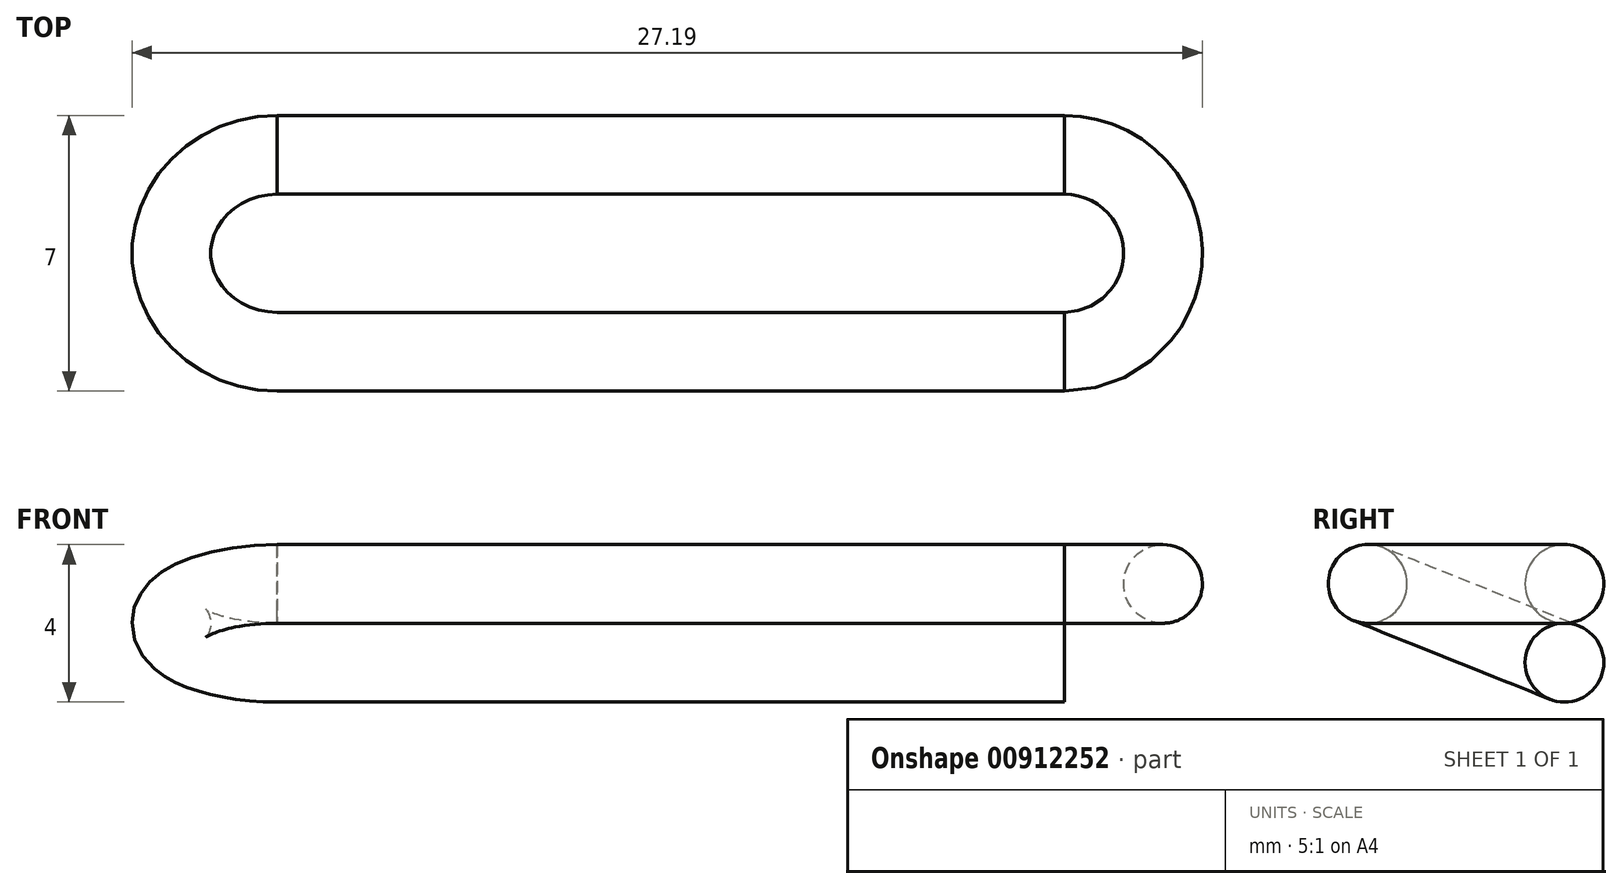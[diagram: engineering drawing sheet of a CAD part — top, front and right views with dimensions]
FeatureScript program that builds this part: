
annotation { "Feature Type Name" : "Feature", "Feature Type Description" : "" }
export const myFeature = defineFeature(function(context is Context, id is Id, definition is map)
    precondition{}
    {
        {
            var Q0;
            Q0=qCreatedBy(makeId("Top.planeOp"),FACE);
            var sketch = newSketch(context, id + "F0", { "sketchPlane" : qUnion([Q0])});
            skCircle(sketch, "E0", {"center": v(-10, 0) * mm, "radius": 2.5 * mm, "construction": true});
            skCircle(sketch, "E1", {"center": v(10, 0) * mm, "radius": 2.5 * mm, "construction": true});
            skLineSegment(sketch, "E2", {"start": v(10, 2.5) * mm, "end": v(-10, 2.5) * mm});
            skSolve(sketch);
        }
        {
            var Q0;
            Q0=qCreatedBy(makeId("Right.planeOp"),FACE);
            cPlane(context, id + "F1", {"entities" : qUnion([Q0]), "cplaneType" : CPlaneType.OFFSET, "offset" : 10 * mm, "oppositeDirection" : true, "width" : 150 * mm, "height" : 150 * mm});
        }
        {
            var Q0;
            Q0=qCreatedBy(id+"F1.planeOp",FACE);
            var sketch = newSketch(context, id + "F2", { "sketchPlane" : qUnion([Q0])});
            skLineSegment(sketch, "E3", {"start": v(2.5, 0) * mm, "end": v(-2.5, 2) * mm, "construction": true});
            skCircle(sketch, "E4", {"center": v(2.5, 0) * mm, "radius": 1 * mm, "construction": true});
            skLineSegment(sketch, "E5", {"start": v(2.5, 0) * mm, "end": v(-2.5, 0) * mm, "construction": true});
            skLineSegment(sketch, "E6", {"start": v(2.5, 1) * mm, "end": v(-3.26, 1) * mm, "construction": true});
            skCircle(sketch, "E7", {"center": v(-2.5, 2) * mm, "radius": 1 * mm, "construction": true});
            skLineSegment(sketch, "E8", {"start": v(-2.5, 0) * mm, "end": v(-2.5, 3.26) * mm, "construction": true});
            skSolve(sketch);
        }
        {
            var Q0;
            Q0=sQuery(id+"F2.wireOp",EDGE,"E3");
            cPlane(context, id + "F3", {"entities" : qUnion([Q0]), "cplaneType" : CPlaneType.LINE_ANGLE, "offset" : 25 * mm, "angle" : 0 * degree, "width" : 150 * mm, "height" : 150 * mm});
        }
        {
            var Q0;
            Q0=qCreatedBy(id+"F3.planeOp",FACE);
            var sketch = newSketch(context, id + "F4", { "sketchPlane" : qUnion([Q0])});
            skArc(sketch, "E9", {"start": v(-10, 3.06) * mm, "mid": v(-12.7, 0.37) * mm, "end": v(-10, -2.32) * mm});
            skLineSegment(sketch, "E10", {"start": v(-10, -2.32) * mm, "end": v(-10, 3.06) * mm, "construction": true});
            skSolve(sketch);
        }
        {
            var Q0;
            Q0=qCreatedBy(makeId("Right.planeOp"),FACE);
            var sketch = newSketch(context, id + "F5", { "sketchPlane" : qUnion([Q0])});
            skCircle(sketch, "E11", {"center": v(2.5, 0) * mm, "radius": 1 * mm});
            skSolve(sketch);
        }
        {
            var Q0;
            Q0=makeQuery(id+"F5.imprint","IMPRINT",FACE,{"disambiguationData":[TD([[makeQuery(id+"F5.imprint","IMPRINT",EDGE,{"derivedFrom":sQuery(id+"F5.wireOp",EDGE,"E11")}),1.0]])]});
            var Q1;
            Q1=sQuery(id+"F0.wireOp",EDGE,"E2");
            var Q2;
            Q2=sQuery(id+"F4.wireOp",EDGE,"E9");
            sweep(context, id + "F6", {"profiles" : qUnion([Q0]), "path" : qUnion([Q1, Q2])});
        }
        {
            var Q0;
            Q0=makeQuery(id+"F6.opSweep","CAP_FACE",FACE,{"disambiguationData":[OSD([sQuery(id+"F4.wireOp",VERTEX,"E9.start"),sQuery(id+"F5.wireOp",EDGE,"E11")])],"isStart":true});
            extrude(context, id + "F7", {"entities" : qUnion([Q0]), "operationType" : NewBodyOperationType.ADD, "depth" : 20 * mm, "offsetDistance" : 25 * mm});
        }
        {
            var Q0;
            Q0=makeQuery(id+"F7.opExtrude","CAP_FACE",FACE,{"disambiguationData":[OSD([sQuery(id+"F4.wireOp",VERTEX,"E9.start"),sQuery(id+"F5.wireOp",EDGE,"E11")])],"isStart":false});
            var sketch = newSketch(context, id + "F8", { "sketchPlane" : qUnion([Q0])});
            skLineSegment(sketch, "E12", {"start": v(-2.5, 2) * mm, "end": v(2.5, 2) * mm, "construction": true});
            skSolve(sketch);
        }
        {
            var Q0;
            Q0=sQuery(id+"F8.wireOp",EDGE,"E12");
            cPlane(context, id + "F9", {"entities" : qUnion([Q0]), "cplaneType" : CPlaneType.LINE_ANGLE, "offset" : 25 * mm, "angle" : 0 * degree, "width" : 150 * mm, "height" : 150 * mm});
        }
        {
            var Q0;
            Q0=qCreatedBy(id+"F9.planeOp",FACE);
            var sketch = newSketch(context, id + "F10", { "sketchPlane" : qUnion([Q0])});
            skArc(sketch, "E13", {"start": v(10, -2.5) * mm, "mid": v(12.5, 0) * mm, "end": v(10, 2.5) * mm});
            skLineSegment(sketch, "E14", {"start": v(10, -3.79) * mm, "end": v(10, 6.07) * mm, "construction": true});
            skSolve(sketch);
        }
        {
            var Q0;
            Q0=makeQuery(id+"F8.imprint","IMPRINT",FACE,{"disambiguationData":[TD([[makeQuery(id+"F8.imprint","IMPRINT",EDGE,{"derivedFrom":makeQuery(id+"F7.opExtrude","CAP_EDGE",EDGE,{"disambiguationData":[OSD([sQuery(id+"F4.wireOp",VERTEX,"E9.start"),sQuery(id+"F5.wireOp",EDGE,"E11")])],"isStart":false})}),-1.0]])]});
            var Q1;
            Q1=sQuery(id+"F10.wireOp",EDGE,"E13");
            sweep(context, id + "F11", {"profiles" : qUnion([Q0]), "path" : qUnion([Q1])});
        }
        {
            var Q0;
            Q0=makeQuery(id+"F11.opSweep","CAP_FACE",FACE,{"disambiguationData":[OSD([sQuery(id+"F4.wireOp",VERTEX,"E9.start"),sQuery(id+"F5.wireOp",EDGE,"E11"),sQuery(id+"F10.wireOp",VERTEX,"E13.end")])],"isStart":false});
            extrude(context, id + "F12", {"entities" : qUnion([Q0]), "depth" : 20 * mm, "offsetDistance" : 25 * mm});
        }
    });
